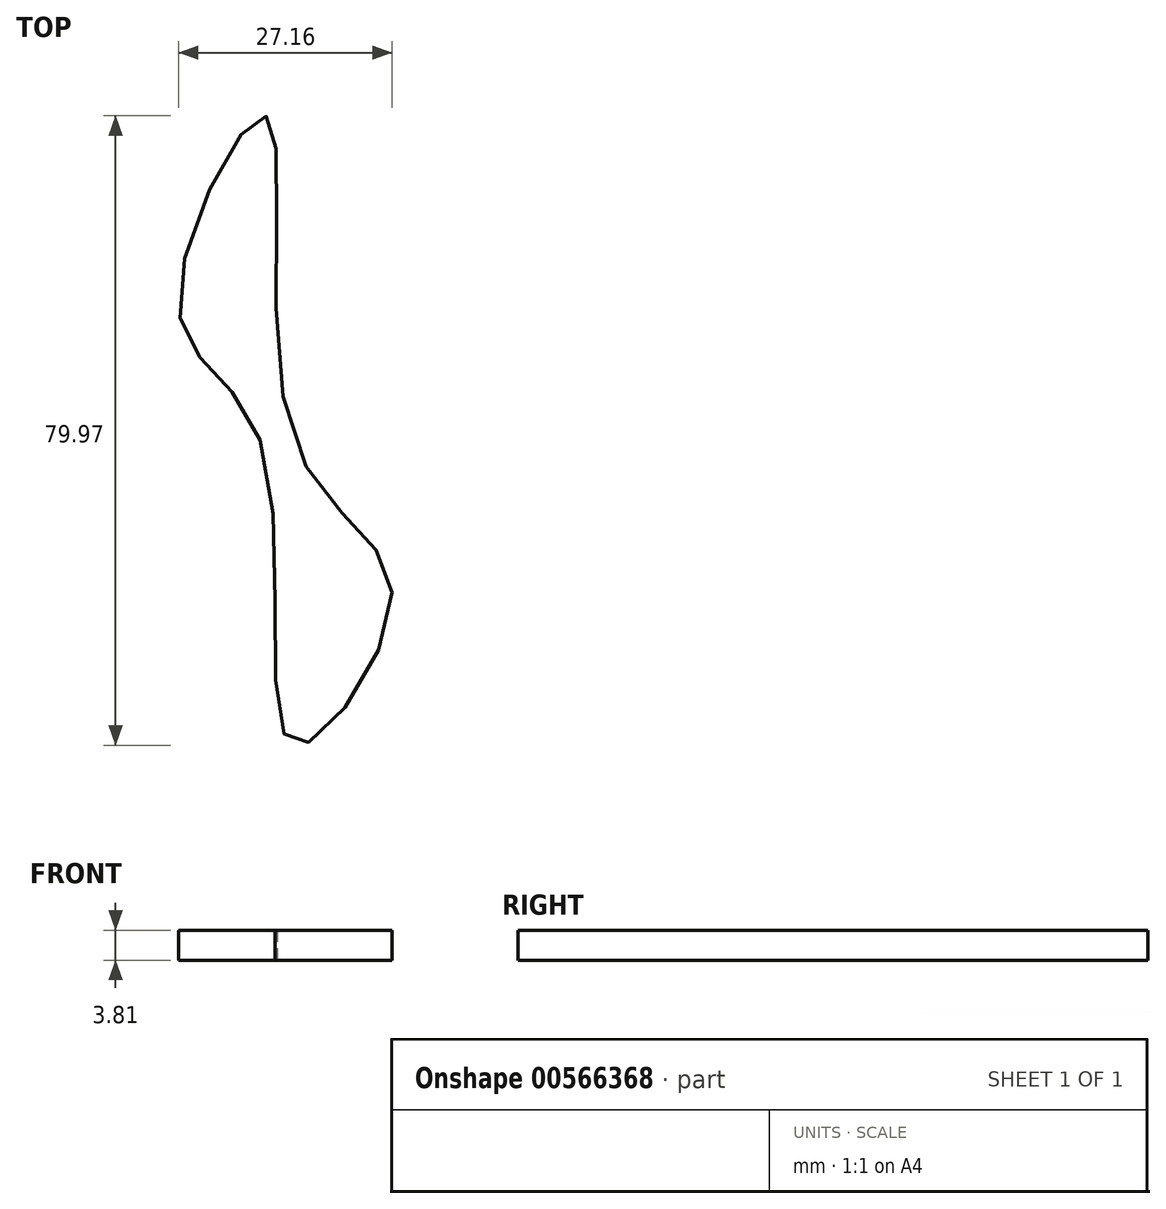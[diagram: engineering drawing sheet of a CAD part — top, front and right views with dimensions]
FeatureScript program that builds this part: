
annotation { "Feature Type Name" : "Feature", "Feature Type Description" : "" }
export const myFeature = defineFeature(function(context is Context, id is Id, definition is map)
    precondition{}
    {
        {
            var Q0;
            Q0=qCreatedBy(makeId("Top.planeOp"),FACE);
            var sketch = newSketch(context, id + "F0", { "sketchPlane" : qUnion([Q0])});
            skFitSpline(sketch, "E0", {"points": [v(-4.27, 0) * mm, v(-14.63, 16.77) * mm, v(-3.66, 41.16) * mm, v(0, 0) * mm, v(12.5, -19.82) * mm, v(0, -38.72) * mm, v(-4.27, 0) * mm]});
            skSolve(sketch);
        }
        {
            var Q0;
            Q0=makeQuery(id+"F0.imprint","IMPRINT",FACE,{"disambiguationData":[TD([[makeQuery(id+"F0.imprint","IMPRINT",EDGE,{"derivedFrom":sQuery(id+"F0.wireOp",EDGE,"E0")}),-1.0]])]});
            extrude(context, id + "F1", {"entities" : qUnion([Q0]), "depth" : 3.8 * mm, "offsetDistance" : 25.4 * mm});
        }
    });
